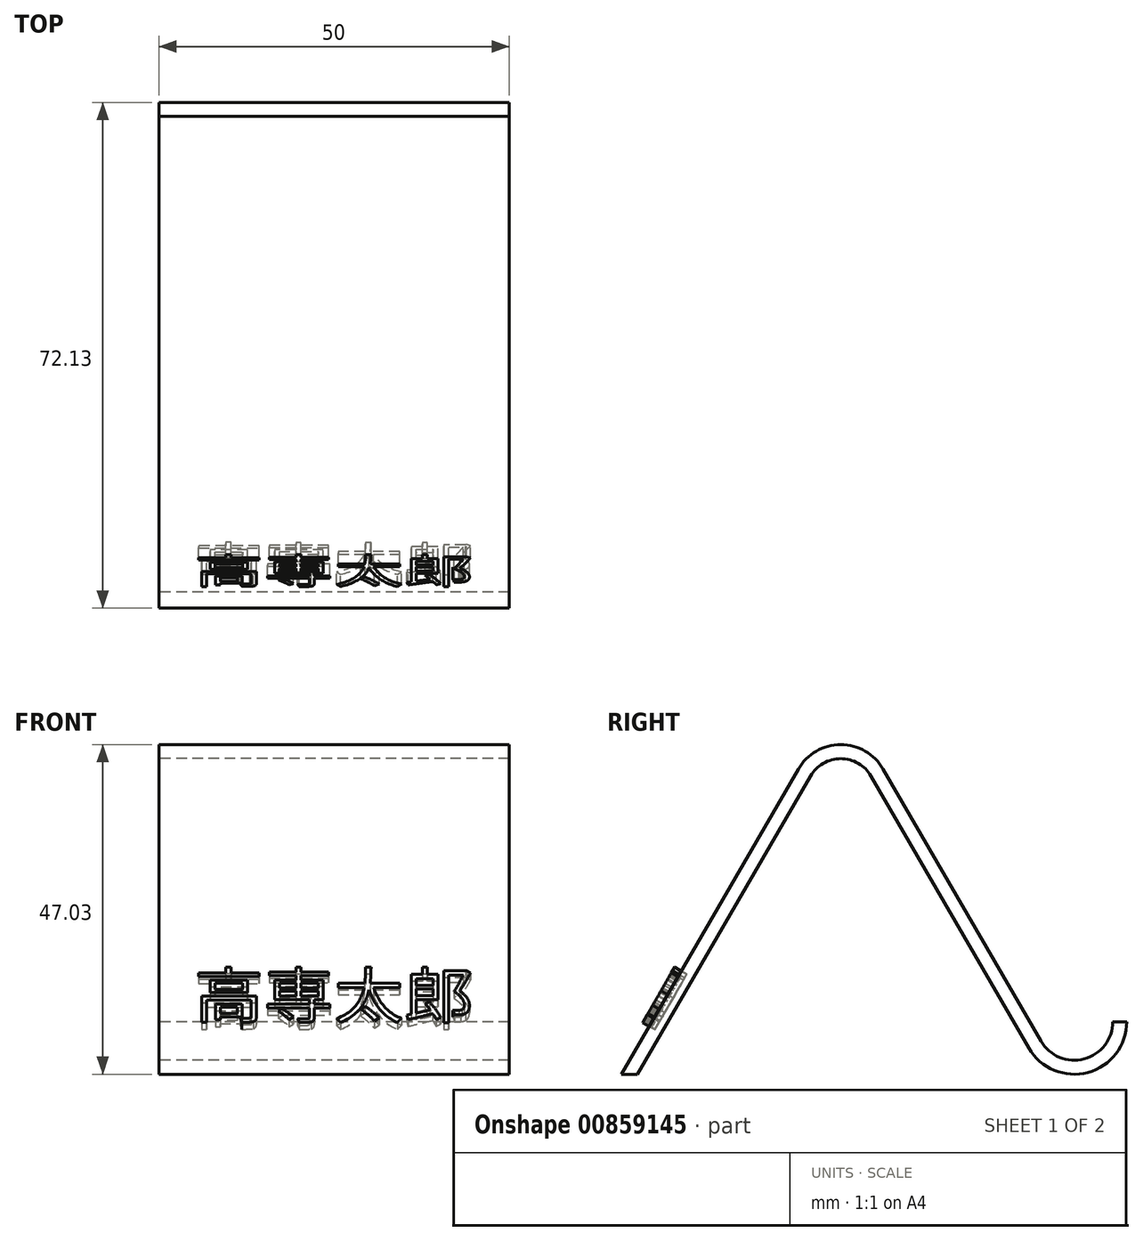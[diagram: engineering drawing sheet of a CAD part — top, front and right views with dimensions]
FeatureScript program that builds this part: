
annotation { "Feature Type Name" : "Feature", "Feature Type Description" : "" }
export const myFeature = defineFeature(function(context is Context, id is Id, definition is map)
    precondition{}
    {
        {
            var Q0;
            Q0=qCreatedBy(makeId("Right.planeOp"),FACE);
            var sketch = newSketch(context, id + "F0", { "sketchPlane" : qUnion([Q0])});
            skLineSegment(sketch, "E0", {"start": v(4.33, 42.54) * mm, "end": v(26.83, 3.74) * mm});
            skArc(sketch, "E1", {"start": v(26.83, 3.74) * mm, "mid": v(35.27, 0.26) * mm, "end": v(40.82, 7.5) * mm});
            skLineSegment(sketch, "E2", {"start": v(0, 61.22) * mm, "end": v(0, -24.36) * mm, "construction": true});
            skLineSegment(sketch, "E3", {"start": v(33.32, 7.5) * mm, "end": v(57.44, 7.5) * mm, "construction": true});
            skLineSegment(sketch, "E4", {"start": v(57.44, 0) * mm, "end": v(-52.05, 0) * mm, "construction": true});
            skLineSegment(sketch, "E5.MirrorCS", {"start": v(-4.33, 42.54) * mm, "end": v(-29, 0) * mm});
            skPoint(sketch, "E6.orphan", {"position": v(29, 0) * mm});
            skPoint(sketch, "E7.visualSharp", {"position": v(0, 50) * mm});
            skArc(sketch, "E7.filletArc", {"start": v(4.33, 42.54) * mm, "mid": v(0, 45.03) * mm, "end": v(-4.33, 42.54) * mm});
            skLineSegment(sketch, "E8.0", {"start": v(-6.06, 43.55) * mm, "end": v(-31.31, 0) * mm});
            skArc(sketch, "E8.1", {"start": v(6.06, 43.55) * mm, "mid": v(0, 47.03) * mm, "end": v(-6.06, 43.55) * mm});
            skLineSegment(sketch, "E8.2", {"start": v(6.06, 43.55) * mm, "end": v(28.56, 4.74) * mm});
            skArc(sketch, "E8.3", {"start": v(28.56, 4.74) * mm, "mid": v(34.75, 2.19) * mm, "end": v(38.82, 7.5) * mm});
            skLineSegment(sketch, "E9", {"start": v(40.82, 7.5) * mm, "end": v(38.82, 7.5) * mm});
            skLineSegment(sketch, "E10", {"start": v(-29, 0) * mm, "end": v(-31.31, 0) * mm});
            skSolve(sketch);
        }
        {
            var Q0;
            Q0 = qSketchRegion(id + "F0", true);
            extrude(context, id + "F1", {"entities" : qUnion([Q0]), "depth" : 50 * mm, "offsetDistance" : 25 * mm});
        }
        {
            var Q0;
            Q0=qCreatedBy(makeId("Front.planeOp"),FACE);
            var sketch = newSketch(context, id + "F2", { "sketchPlane" : qUnion([Q0])});
            skText(sketch, "E11", { "text": "高専太郎", "fontName": "NotoSansCJKjp-Regular.otf"});
            skLineSegment(sketch, "E12", {"start": v(25, 0) * mm, "end": v(25, 5) * mm, "construction": true});
            const initialGuessF2  = {"E11": [0.005, 0.00491, 1, 0, 0.00719]};
            skSetInitialGuess(sketch, initialGuessF2);
            skSolve(sketch);
        }
        {
            var Q0;
            Q0 = qSketchRegion(id + "F2", true);
            extrude(context, id + "F3", {"entities" : qUnion([Q0]), "depth" : 2 * mm, "offsetDistance" : 25 * mm});
        }
        {
            var Q0;
            Q0=makeQuery(id+"F3.opExtrude","SWEPT_BODY",BODY,{"disambiguationData":[OSD([sQuery(id+"F2.wireOp",EDGE,"E11.sketch_text.stroke-0"),sQuery(id+"F2.wireOp",EDGE,"E11.sketch_text.stroke-1"),sQuery(id+"F2.wireOp",EDGE,"E11.sketch_text.stroke-2"),sQuery(id+"F2.wireOp",EDGE,"E11.sketch_text.stroke-3"),sQuery(id+"F2.wireOp",EDGE,"E11.sketch_text.stroke-4"),sQuery(id+"F2.wireOp",EDGE,"E11.sketch_text.stroke-5"),sQuery(id+"F2.wireOp",EDGE,"E11.sketch_text.stroke-6"),sQuery(id+"F2.wireOp",EDGE,"E11.sketch_text.stroke-7"),sQuery(id+"F2.wireOp",EDGE,"E11.sketch_text.stroke-8"),sQuery(id+"F2.wireOp",EDGE,"E11.sketch_text.stroke-9")])]});
            var Q1;
            Q1=makeQuery(id+"F3.opExtrude","SWEPT_BODY",BODY,{"disambiguationData":[OSD([sQuery(id+"F2.wireOp",EDGE,"E11.sketch_text.stroke-10"),sQuery(id+"F2.wireOp",EDGE,"E11.sketch_text.stroke-11"),sQuery(id+"F2.wireOp",EDGE,"E11.sketch_text.stroke-12"),sQuery(id+"F2.wireOp",EDGE,"E11.sketch_text.stroke-13"),sQuery(id+"F2.wireOp",EDGE,"E11.sketch_text.stroke-14"),sQuery(id+"F2.wireOp",EDGE,"E11.sketch_text.stroke-15"),sQuery(id+"F2.wireOp",EDGE,"E11.sketch_text.stroke-16"),sQuery(id+"F2.wireOp",EDGE,"E11.sketch_text.stroke-17"),sQuery(id+"F2.wireOp",EDGE,"E11.sketch_text.stroke-18"),sQuery(id+"F2.wireOp",EDGE,"E11.sketch_text.stroke-19"),sQuery(id+"F2.wireOp",EDGE,"E11.sketch_text.stroke-20"),sQuery(id+"F2.wireOp",EDGE,"E11.sketch_text.stroke-21")])]});
            var Q2;
            Q2=makeQuery(id+"F3.opExtrude","SWEPT_BODY",BODY,{"disambiguationData":[OSD([sQuery(id+"F2.wireOp",EDGE,"E11.sketch_text.stroke-22"),sQuery(id+"F2.wireOp",EDGE,"E11.sketch_text.stroke-23"),sQuery(id+"F2.wireOp",EDGE,"E11.sketch_text.stroke-24"),sQuery(id+"F2.wireOp",EDGE,"E11.sketch_text.stroke-25"),sQuery(id+"F2.wireOp",EDGE,"E11.sketch_text.stroke-26"),sQuery(id+"F2.wireOp",EDGE,"E11.sketch_text.stroke-27"),sQuery(id+"F2.wireOp",EDGE,"E11.sketch_text.stroke-28"),sQuery(id+"F2.wireOp",EDGE,"E11.sketch_text.stroke-29")])]});
            var Q3;
            Q3=makeQuery(id+"F3.opExtrude","SWEPT_BODY",BODY,{"disambiguationData":[OSD([sQuery(id+"F2.wireOp",EDGE,"E11.sketch_text.stroke-30"),sQuery(id+"F2.wireOp",EDGE,"E11.sketch_text.stroke-31"),sQuery(id+"F2.wireOp",EDGE,"E11.sketch_text.stroke-32"),sQuery(id+"F2.wireOp",EDGE,"E11.sketch_text.stroke-33"),sQuery(id+"F2.wireOp",EDGE,"E11.sketch_text.stroke-34"),sQuery(id+"F2.wireOp",EDGE,"E11.sketch_text.stroke-35"),sQuery(id+"F2.wireOp",EDGE,"E11.sketch_text.stroke-36"),sQuery(id+"F2.wireOp",EDGE,"E11.sketch_text.stroke-37")])]});
            var Q4;
            Q4=makeQuery(id+"F3.opExtrude","SWEPT_BODY",BODY,{"disambiguationData":[OSD([sQuery(id+"F2.wireOp",EDGE,"E11.sketch_text.stroke-38"),sQuery(id+"F2.wireOp",EDGE,"E11.sketch_text.stroke-39"),sQuery(id+"F2.wireOp",EDGE,"E11.sketch_text.stroke-40"),sQuery(id+"F2.wireOp",EDGE,"E11.sketch_text.stroke-41")])]});
            var Q5;
            Q5=makeQuery(id+"F3.opExtrude","SWEPT_BODY",BODY,{"disambiguationData":[OSD([sQuery(id+"F2.wireOp",EDGE,"E11.sketch_text.stroke-42"),sQuery(id+"F2.wireOp",EDGE,"E11.sketch_text.stroke-43"),sQuery(id+"F2.wireOp",EDGE,"E11.sketch_text.stroke-44"),sQuery(id+"F2.wireOp",EDGE,"E11.sketch_text.stroke-45"),sQuery(id+"F2.wireOp",EDGE,"E11.sketch_text.stroke-46"),sQuery(id+"F2.wireOp",EDGE,"E11.sketch_text.stroke-47"),sQuery(id+"F2.wireOp",EDGE,"E11.sketch_text.stroke-48"),sQuery(id+"F2.wireOp",EDGE,"E11.sketch_text.stroke-49"),sQuery(id+"F2.wireOp",EDGE,"E11.sketch_text.stroke-50"),sQuery(id+"F2.wireOp",EDGE,"E11.sketch_text.stroke-51"),sQuery(id+"F2.wireOp",EDGE,"E11.sketch_text.stroke-52"),sQuery(id+"F2.wireOp",EDGE,"E11.sketch_text.stroke-53"),sQuery(id+"F2.wireOp",EDGE,"E11.sketch_text.stroke-54"),sQuery(id+"F2.wireOp",EDGE,"E11.sketch_text.stroke-55"),sQuery(id+"F2.wireOp",EDGE,"E11.sketch_text.stroke-56"),sQuery(id+"F2.wireOp",EDGE,"E11.sketch_text.stroke-57"),sQuery(id+"F2.wireOp",EDGE,"E11.sketch_text.stroke-58"),sQuery(id+"F2.wireOp",EDGE,"E11.sketch_text.stroke-59"),sQuery(id+"F2.wireOp",EDGE,"E11.sketch_text.stroke-60"),sQuery(id+"F2.wireOp",EDGE,"E11.sketch_text.stroke-61"),sQuery(id+"F2.wireOp",EDGE,"E11.sketch_text.stroke-62"),sQuery(id+"F2.wireOp",EDGE,"E11.sketch_text.stroke-63"),sQuery(id+"F2.wireOp",EDGE,"E11.sketch_text.stroke-64"),sQuery(id+"F2.wireOp",EDGE,"E11.sketch_text.stroke-65"),sQuery(id+"F2.wireOp",EDGE,"E11.sketch_text.stroke-66"),sQuery(id+"F2.wireOp",EDGE,"E11.sketch_text.stroke-67"),sQuery(id+"F2.wireOp",EDGE,"E11.sketch_text.stroke-68"),sQuery(id+"F2.wireOp",EDGE,"E11.sketch_text.stroke-69"),sQuery(id+"F2.wireOp",EDGE,"E11.sketch_text.stroke-70"),sQuery(id+"F2.wireOp",EDGE,"E11.sketch_text.stroke-71"),sQuery(id+"F2.wireOp",EDGE,"E11.sketch_text.stroke-72"),sQuery(id+"F2.wireOp",EDGE,"E11.sketch_text.stroke-73"),sQuery(id+"F2.wireOp",EDGE,"E11.sketch_text.stroke-74"),sQuery(id+"F2.wireOp",EDGE,"E11.sketch_text.stroke-75"),sQuery(id+"F2.wireOp",EDGE,"E11.sketch_text.stroke-76"),sQuery(id+"F2.wireOp",EDGE,"E11.sketch_text.stroke-77"),sQuery(id+"F2.wireOp",EDGE,"E11.sketch_text.stroke-78"),sQuery(id+"F2.wireOp",EDGE,"E11.sketch_text.stroke-79"),sQuery(id+"F2.wireOp",EDGE,"E11.sketch_text.stroke-80"),sQuery(id+"F2.wireOp",EDGE,"E11.sketch_text.stroke-81"),sQuery(id+"F2.wireOp",EDGE,"E11.sketch_text.stroke-82"),sQuery(id+"F2.wireOp",EDGE,"E11.sketch_text.stroke-83"),sQuery(id+"F2.wireOp",EDGE,"E11.sketch_text.stroke-84"),sQuery(id+"F2.wireOp",EDGE,"E11.sketch_text.stroke-85"),sQuery(id+"F2.wireOp",EDGE,"E11.sketch_text.stroke-86"),sQuery(id+"F2.wireOp",EDGE,"E11.sketch_text.stroke-87"),sQuery(id+"F2.wireOp",EDGE,"E11.sketch_text.stroke-88"),sQuery(id+"F2.wireOp",EDGE,"E11.sketch_text.stroke-89")])]});
            var Q6;
            Q6=makeQuery(id+"F3.opExtrude","SWEPT_BODY",BODY,{"disambiguationData":[OSD([sQuery(id+"F2.wireOp",EDGE,"E11.sketch_text.stroke-90"),sQuery(id+"F2.wireOp",EDGE,"E11.sketch_text.stroke-91"),sQuery(id+"F2.wireOp",EDGE,"E11.sketch_text.stroke-92"),sQuery(id+"F2.wireOp",EDGE,"E11.sketch_text.stroke-93")])]});
            var Q7;
            Q7=makeQuery(id+"F3.opExtrude","SWEPT_BODY",BODY,{"disambiguationData":[OSD([sQuery(id+"F2.wireOp",EDGE,"E11.sketch_text.stroke-94"),sQuery(id+"F2.wireOp",EDGE,"E11.sketch_text.stroke-95"),sQuery(id+"F2.wireOp",EDGE,"E11.sketch_text.stroke-96"),sQuery(id+"F2.wireOp",EDGE,"E11.sketch_text.stroke-97"),sQuery(id+"F2.wireOp",EDGE,"E11.sketch_text.stroke-98"),sQuery(id+"F2.wireOp",EDGE,"E11.sketch_text.stroke-99"),sQuery(id+"F2.wireOp",EDGE,"E11.sketch_text.stroke-100"),sQuery(id+"F2.wireOp",EDGE,"E11.sketch_text.stroke-101"),sQuery(id+"F2.wireOp",EDGE,"E11.sketch_text.stroke-102"),sQuery(id+"F2.wireOp",EDGE,"E11.sketch_text.stroke-103"),sQuery(id+"F2.wireOp",EDGE,"E11.sketch_text.stroke-104"),sQuery(id+"F2.wireOp",EDGE,"E11.sketch_text.stroke-105"),sQuery(id+"F2.wireOp",EDGE,"E11.sketch_text.stroke-106"),sQuery(id+"F2.wireOp",EDGE,"E11.sketch_text.stroke-107"),sQuery(id+"F2.wireOp",EDGE,"E11.sketch_text.stroke-108")])]});
            var Q8;
            Q8=makeQuery(id+"F3.opExtrude","SWEPT_BODY",BODY,{"disambiguationData":[OSD([sQuery(id+"F2.wireOp",EDGE,"E11.sketch_text.stroke-109"),sQuery(id+"F2.wireOp",EDGE,"E11.sketch_text.stroke-110"),sQuery(id+"F2.wireOp",EDGE,"E11.sketch_text.stroke-111"),sQuery(id+"F2.wireOp",EDGE,"E11.sketch_text.stroke-112"),sQuery(id+"F2.wireOp",EDGE,"E11.sketch_text.stroke-113"),sQuery(id+"F2.wireOp",EDGE,"E11.sketch_text.stroke-114"),sQuery(id+"F2.wireOp",EDGE,"E11.sketch_text.stroke-115"),sQuery(id+"F2.wireOp",EDGE,"E11.sketch_text.stroke-116"),sQuery(id+"F2.wireOp",EDGE,"E11.sketch_text.stroke-117"),sQuery(id+"F2.wireOp",EDGE,"E11.sketch_text.stroke-118"),sQuery(id+"F2.wireOp",EDGE,"E11.sketch_text.stroke-119"),sQuery(id+"F2.wireOp",EDGE,"E11.sketch_text.stroke-120"),sQuery(id+"F2.wireOp",EDGE,"E11.sketch_text.stroke-121"),sQuery(id+"F2.wireOp",EDGE,"E11.sketch_text.stroke-122"),sQuery(id+"F2.wireOp",EDGE,"E11.sketch_text.stroke-123"),sQuery(id+"F2.wireOp",EDGE,"E11.sketch_text.stroke-124"),sQuery(id+"F2.wireOp",EDGE,"E11.sketch_text.stroke-125"),sQuery(id+"F2.wireOp",EDGE,"E11.sketch_text.stroke-126"),sQuery(id+"F2.wireOp",EDGE,"E11.sketch_text.stroke-127"),sQuery(id+"F2.wireOp",EDGE,"E11.sketch_text.stroke-128"),sQuery(id+"F2.wireOp",EDGE,"E11.sketch_text.stroke-129"),sQuery(id+"F2.wireOp",EDGE,"E11.sketch_text.stroke-130"),sQuery(id+"F2.wireOp",EDGE,"E11.sketch_text.stroke-131"),sQuery(id+"F2.wireOp",EDGE,"E11.sketch_text.stroke-132"),sQuery(id+"F2.wireOp",EDGE,"E11.sketch_text.stroke-133"),sQuery(id+"F2.wireOp",EDGE,"E11.sketch_text.stroke-134")])]});
            var Q9;
            Q9=makeQuery(id+"F3.opExtrude","SWEPT_BODY",BODY,{"disambiguationData":[OSD([sQuery(id+"F2.wireOp",EDGE,"E11.sketch_text.stroke-135"),sQuery(id+"F2.wireOp",EDGE,"E11.sketch_text.stroke-136"),sQuery(id+"F2.wireOp",EDGE,"E11.sketch_text.stroke-137"),sQuery(id+"F2.wireOp",EDGE,"E11.sketch_text.stroke-138"),sQuery(id+"F2.wireOp",EDGE,"E11.sketch_text.stroke-139"),sQuery(id+"F2.wireOp",EDGE,"E11.sketch_text.stroke-140"),sQuery(id+"F2.wireOp",EDGE,"E11.sketch_text.stroke-141"),sQuery(id+"F2.wireOp",EDGE,"E11.sketch_text.stroke-142"),sQuery(id+"F2.wireOp",EDGE,"E11.sketch_text.stroke-143"),sQuery(id+"F2.wireOp",EDGE,"E11.sketch_text.stroke-144"),sQuery(id+"F2.wireOp",EDGE,"E11.sketch_text.stroke-145"),sQuery(id+"F2.wireOp",EDGE,"E11.sketch_text.stroke-146"),sQuery(id+"F2.wireOp",EDGE,"E11.sketch_text.stroke-147"),sQuery(id+"F2.wireOp",EDGE,"E11.sketch_text.stroke-148"),sQuery(id+"F2.wireOp",EDGE,"E11.sketch_text.stroke-149"),sQuery(id+"F2.wireOp",EDGE,"E11.sketch_text.stroke-150"),sQuery(id+"F2.wireOp",EDGE,"E11.sketch_text.stroke-151"),sQuery(id+"F2.wireOp",EDGE,"E11.sketch_text.stroke-152")])]});
            var Q10;
            Q10=makeQuery(id+"F1.opExtrude","SWEPT_EDGE",EDGE,{"disambiguationData":[OSD([sQuery(id+"F0.wireOp",EDGE,"E8.0"),sQuery(id+"F0.wireOp",EDGE,"E8.1")])]});
            transform(context, id + "F4", {"entities" : qUnion([Q0, Q1, Q2, Q3, Q4, Q5, Q6, Q7, Q8, Q9]), "transformType" : TransformType.ROTATION, "transformAxis" : qUnion([Q10]), "angle" : 30 * degree, "makeCopy" : false});
        }
        {
            var Q0;
            Q0=makeQuery(id+"F3.opExtrude","SWEPT_BODY",BODY,{"disambiguationData":[OSD([sQuery(id+"F2.wireOp",EDGE,"E11.sketch_text.stroke-0"),sQuery(id+"F2.wireOp",EDGE,"E11.sketch_text.stroke-1"),sQuery(id+"F2.wireOp",EDGE,"E11.sketch_text.stroke-2"),sQuery(id+"F2.wireOp",EDGE,"E11.sketch_text.stroke-3"),sQuery(id+"F2.wireOp",EDGE,"E11.sketch_text.stroke-4"),sQuery(id+"F2.wireOp",EDGE,"E11.sketch_text.stroke-5"),sQuery(id+"F2.wireOp",EDGE,"E11.sketch_text.stroke-6"),sQuery(id+"F2.wireOp",EDGE,"E11.sketch_text.stroke-7"),sQuery(id+"F2.wireOp",EDGE,"E11.sketch_text.stroke-8"),sQuery(id+"F2.wireOp",EDGE,"E11.sketch_text.stroke-9")])]});
            var Q1;
            Q1=makeQuery(id+"F3.opExtrude","SWEPT_BODY",BODY,{"disambiguationData":[OSD([sQuery(id+"F2.wireOp",EDGE,"E11.sketch_text.stroke-10"),sQuery(id+"F2.wireOp",EDGE,"E11.sketch_text.stroke-11"),sQuery(id+"F2.wireOp",EDGE,"E11.sketch_text.stroke-12"),sQuery(id+"F2.wireOp",EDGE,"E11.sketch_text.stroke-13"),sQuery(id+"F2.wireOp",EDGE,"E11.sketch_text.stroke-14"),sQuery(id+"F2.wireOp",EDGE,"E11.sketch_text.stroke-15"),sQuery(id+"F2.wireOp",EDGE,"E11.sketch_text.stroke-16"),sQuery(id+"F2.wireOp",EDGE,"E11.sketch_text.stroke-17"),sQuery(id+"F2.wireOp",EDGE,"E11.sketch_text.stroke-18"),sQuery(id+"F2.wireOp",EDGE,"E11.sketch_text.stroke-19"),sQuery(id+"F2.wireOp",EDGE,"E11.sketch_text.stroke-20"),sQuery(id+"F2.wireOp",EDGE,"E11.sketch_text.stroke-21")])]});
            var Q2;
            Q2=makeQuery(id+"F3.opExtrude","SWEPT_BODY",BODY,{"disambiguationData":[OSD([sQuery(id+"F2.wireOp",EDGE,"E11.sketch_text.stroke-22"),sQuery(id+"F2.wireOp",EDGE,"E11.sketch_text.stroke-23"),sQuery(id+"F2.wireOp",EDGE,"E11.sketch_text.stroke-24"),sQuery(id+"F2.wireOp",EDGE,"E11.sketch_text.stroke-25"),sQuery(id+"F2.wireOp",EDGE,"E11.sketch_text.stroke-26"),sQuery(id+"F2.wireOp",EDGE,"E11.sketch_text.stroke-27"),sQuery(id+"F2.wireOp",EDGE,"E11.sketch_text.stroke-28"),sQuery(id+"F2.wireOp",EDGE,"E11.sketch_text.stroke-29")])]});
            var Q3;
            Q3=makeQuery(id+"F3.opExtrude","SWEPT_BODY",BODY,{"disambiguationData":[OSD([sQuery(id+"F2.wireOp",EDGE,"E11.sketch_text.stroke-30"),sQuery(id+"F2.wireOp",EDGE,"E11.sketch_text.stroke-31"),sQuery(id+"F2.wireOp",EDGE,"E11.sketch_text.stroke-32"),sQuery(id+"F2.wireOp",EDGE,"E11.sketch_text.stroke-33"),sQuery(id+"F2.wireOp",EDGE,"E11.sketch_text.stroke-34"),sQuery(id+"F2.wireOp",EDGE,"E11.sketch_text.stroke-35"),sQuery(id+"F2.wireOp",EDGE,"E11.sketch_text.stroke-36"),sQuery(id+"F2.wireOp",EDGE,"E11.sketch_text.stroke-37")])]});
            var Q4;
            Q4=makeQuery(id+"F3.opExtrude","SWEPT_BODY",BODY,{"disambiguationData":[OSD([sQuery(id+"F2.wireOp",EDGE,"E11.sketch_text.stroke-38"),sQuery(id+"F2.wireOp",EDGE,"E11.sketch_text.stroke-39"),sQuery(id+"F2.wireOp",EDGE,"E11.sketch_text.stroke-40"),sQuery(id+"F2.wireOp",EDGE,"E11.sketch_text.stroke-41")])]});
            var Q5;
            Q5=makeQuery(id+"F3.opExtrude","SWEPT_BODY",BODY,{"disambiguationData":[OSD([sQuery(id+"F2.wireOp",EDGE,"E11.sketch_text.stroke-42"),sQuery(id+"F2.wireOp",EDGE,"E11.sketch_text.stroke-43"),sQuery(id+"F2.wireOp",EDGE,"E11.sketch_text.stroke-44"),sQuery(id+"F2.wireOp",EDGE,"E11.sketch_text.stroke-45"),sQuery(id+"F2.wireOp",EDGE,"E11.sketch_text.stroke-46"),sQuery(id+"F2.wireOp",EDGE,"E11.sketch_text.stroke-47"),sQuery(id+"F2.wireOp",EDGE,"E11.sketch_text.stroke-48"),sQuery(id+"F2.wireOp",EDGE,"E11.sketch_text.stroke-49"),sQuery(id+"F2.wireOp",EDGE,"E11.sketch_text.stroke-50"),sQuery(id+"F2.wireOp",EDGE,"E11.sketch_text.stroke-51"),sQuery(id+"F2.wireOp",EDGE,"E11.sketch_text.stroke-52"),sQuery(id+"F2.wireOp",EDGE,"E11.sketch_text.stroke-53"),sQuery(id+"F2.wireOp",EDGE,"E11.sketch_text.stroke-54"),sQuery(id+"F2.wireOp",EDGE,"E11.sketch_text.stroke-55"),sQuery(id+"F2.wireOp",EDGE,"E11.sketch_text.stroke-56"),sQuery(id+"F2.wireOp",EDGE,"E11.sketch_text.stroke-57"),sQuery(id+"F2.wireOp",EDGE,"E11.sketch_text.stroke-58"),sQuery(id+"F2.wireOp",EDGE,"E11.sketch_text.stroke-59"),sQuery(id+"F2.wireOp",EDGE,"E11.sketch_text.stroke-60"),sQuery(id+"F2.wireOp",EDGE,"E11.sketch_text.stroke-61"),sQuery(id+"F2.wireOp",EDGE,"E11.sketch_text.stroke-62"),sQuery(id+"F2.wireOp",EDGE,"E11.sketch_text.stroke-63"),sQuery(id+"F2.wireOp",EDGE,"E11.sketch_text.stroke-64"),sQuery(id+"F2.wireOp",EDGE,"E11.sketch_text.stroke-65"),sQuery(id+"F2.wireOp",EDGE,"E11.sketch_text.stroke-66"),sQuery(id+"F2.wireOp",EDGE,"E11.sketch_text.stroke-67"),sQuery(id+"F2.wireOp",EDGE,"E11.sketch_text.stroke-68"),sQuery(id+"F2.wireOp",EDGE,"E11.sketch_text.stroke-69"),sQuery(id+"F2.wireOp",EDGE,"E11.sketch_text.stroke-70"),sQuery(id+"F2.wireOp",EDGE,"E11.sketch_text.stroke-71"),sQuery(id+"F2.wireOp",EDGE,"E11.sketch_text.stroke-72"),sQuery(id+"F2.wireOp",EDGE,"E11.sketch_text.stroke-73"),sQuery(id+"F2.wireOp",EDGE,"E11.sketch_text.stroke-74"),sQuery(id+"F2.wireOp",EDGE,"E11.sketch_text.stroke-75"),sQuery(id+"F2.wireOp",EDGE,"E11.sketch_text.stroke-76"),sQuery(id+"F2.wireOp",EDGE,"E11.sketch_text.stroke-77"),sQuery(id+"F2.wireOp",EDGE,"E11.sketch_text.stroke-78"),sQuery(id+"F2.wireOp",EDGE,"E11.sketch_text.stroke-79"),sQuery(id+"F2.wireOp",EDGE,"E11.sketch_text.stroke-80"),sQuery(id+"F2.wireOp",EDGE,"E11.sketch_text.stroke-81"),sQuery(id+"F2.wireOp",EDGE,"E11.sketch_text.stroke-82"),sQuery(id+"F2.wireOp",EDGE,"E11.sketch_text.stroke-83"),sQuery(id+"F2.wireOp",EDGE,"E11.sketch_text.stroke-84"),sQuery(id+"F2.wireOp",EDGE,"E11.sketch_text.stroke-85"),sQuery(id+"F2.wireOp",EDGE,"E11.sketch_text.stroke-86"),sQuery(id+"F2.wireOp",EDGE,"E11.sketch_text.stroke-87"),sQuery(id+"F2.wireOp",EDGE,"E11.sketch_text.stroke-88"),sQuery(id+"F2.wireOp",EDGE,"E11.sketch_text.stroke-89")])]});
            var Q6;
            Q6=makeQuery(id+"F3.opExtrude","SWEPT_BODY",BODY,{"disambiguationData":[OSD([sQuery(id+"F2.wireOp",EDGE,"E11.sketch_text.stroke-90"),sQuery(id+"F2.wireOp",EDGE,"E11.sketch_text.stroke-91"),sQuery(id+"F2.wireOp",EDGE,"E11.sketch_text.stroke-92"),sQuery(id+"F2.wireOp",EDGE,"E11.sketch_text.stroke-93")])]});
            var Q7;
            Q7=makeQuery(id+"F3.opExtrude","SWEPT_BODY",BODY,{"disambiguationData":[OSD([sQuery(id+"F2.wireOp",EDGE,"E11.sketch_text.stroke-94"),sQuery(id+"F2.wireOp",EDGE,"E11.sketch_text.stroke-95"),sQuery(id+"F2.wireOp",EDGE,"E11.sketch_text.stroke-96"),sQuery(id+"F2.wireOp",EDGE,"E11.sketch_text.stroke-97"),sQuery(id+"F2.wireOp",EDGE,"E11.sketch_text.stroke-98"),sQuery(id+"F2.wireOp",EDGE,"E11.sketch_text.stroke-99"),sQuery(id+"F2.wireOp",EDGE,"E11.sketch_text.stroke-100"),sQuery(id+"F2.wireOp",EDGE,"E11.sketch_text.stroke-101"),sQuery(id+"F2.wireOp",EDGE,"E11.sketch_text.stroke-102"),sQuery(id+"F2.wireOp",EDGE,"E11.sketch_text.stroke-103"),sQuery(id+"F2.wireOp",EDGE,"E11.sketch_text.stroke-104"),sQuery(id+"F2.wireOp",EDGE,"E11.sketch_text.stroke-105"),sQuery(id+"F2.wireOp",EDGE,"E11.sketch_text.stroke-106"),sQuery(id+"F2.wireOp",EDGE,"E11.sketch_text.stroke-107"),sQuery(id+"F2.wireOp",EDGE,"E11.sketch_text.stroke-108")])]});
            var Q8;
            Q8=makeQuery(id+"F3.opExtrude","SWEPT_BODY",BODY,{"disambiguationData":[OSD([sQuery(id+"F2.wireOp",EDGE,"E11.sketch_text.stroke-109"),sQuery(id+"F2.wireOp",EDGE,"E11.sketch_text.stroke-110"),sQuery(id+"F2.wireOp",EDGE,"E11.sketch_text.stroke-111"),sQuery(id+"F2.wireOp",EDGE,"E11.sketch_text.stroke-112"),sQuery(id+"F2.wireOp",EDGE,"E11.sketch_text.stroke-113"),sQuery(id+"F2.wireOp",EDGE,"E11.sketch_text.stroke-114"),sQuery(id+"F2.wireOp",EDGE,"E11.sketch_text.stroke-115"),sQuery(id+"F2.wireOp",EDGE,"E11.sketch_text.stroke-116"),sQuery(id+"F2.wireOp",EDGE,"E11.sketch_text.stroke-117"),sQuery(id+"F2.wireOp",EDGE,"E11.sketch_text.stroke-118"),sQuery(id+"F2.wireOp",EDGE,"E11.sketch_text.stroke-119"),sQuery(id+"F2.wireOp",EDGE,"E11.sketch_text.stroke-120"),sQuery(id+"F2.wireOp",EDGE,"E11.sketch_text.stroke-121"),sQuery(id+"F2.wireOp",EDGE,"E11.sketch_text.stroke-122"),sQuery(id+"F2.wireOp",EDGE,"E11.sketch_text.stroke-123"),sQuery(id+"F2.wireOp",EDGE,"E11.sketch_text.stroke-124"),sQuery(id+"F2.wireOp",EDGE,"E11.sketch_text.stroke-125"),sQuery(id+"F2.wireOp",EDGE,"E11.sketch_text.stroke-126"),sQuery(id+"F2.wireOp",EDGE,"E11.sketch_text.stroke-127"),sQuery(id+"F2.wireOp",EDGE,"E11.sketch_text.stroke-128"),sQuery(id+"F2.wireOp",EDGE,"E11.sketch_text.stroke-129"),sQuery(id+"F2.wireOp",EDGE,"E11.sketch_text.stroke-130"),sQuery(id+"F2.wireOp",EDGE,"E11.sketch_text.stroke-131"),sQuery(id+"F2.wireOp",EDGE,"E11.sketch_text.stroke-132"),sQuery(id+"F2.wireOp",EDGE,"E11.sketch_text.stroke-133"),sQuery(id+"F2.wireOp",EDGE,"E11.sketch_text.stroke-134")])]});
            var Q9;
            Q9=makeQuery(id+"F3.opExtrude","SWEPT_BODY",BODY,{"disambiguationData":[OSD([sQuery(id+"F2.wireOp",EDGE,"E11.sketch_text.stroke-135"),sQuery(id+"F2.wireOp",EDGE,"E11.sketch_text.stroke-136"),sQuery(id+"F2.wireOp",EDGE,"E11.sketch_text.stroke-137"),sQuery(id+"F2.wireOp",EDGE,"E11.sketch_text.stroke-138"),sQuery(id+"F2.wireOp",EDGE,"E11.sketch_text.stroke-139"),sQuery(id+"F2.wireOp",EDGE,"E11.sketch_text.stroke-140"),sQuery(id+"F2.wireOp",EDGE,"E11.sketch_text.stroke-141"),sQuery(id+"F2.wireOp",EDGE,"E11.sketch_text.stroke-142"),sQuery(id+"F2.wireOp",EDGE,"E11.sketch_text.stroke-143"),sQuery(id+"F2.wireOp",EDGE,"E11.sketch_text.stroke-144"),sQuery(id+"F2.wireOp",EDGE,"E11.sketch_text.stroke-145"),sQuery(id+"F2.wireOp",EDGE,"E11.sketch_text.stroke-146"),sQuery(id+"F2.wireOp",EDGE,"E11.sketch_text.stroke-147"),sQuery(id+"F2.wireOp",EDGE,"E11.sketch_text.stroke-148"),sQuery(id+"F2.wireOp",EDGE,"E11.sketch_text.stroke-149"),sQuery(id+"F2.wireOp",EDGE,"E11.sketch_text.stroke-150"),sQuery(id+"F2.wireOp",EDGE,"E11.sketch_text.stroke-151"),sQuery(id+"F2.wireOp",EDGE,"E11.sketch_text.stroke-152")])]});
            transform(context, id + "F5", {"entities" : qUnion([Q0, Q1, Q2, Q3, Q4, Q5, Q6, Q7, Q8, Q9]), "transformType" : TransformType.TRANSLATION_3D, "dx" : 0 * mm, "dy" : -6 * mm, "dz" : 0 * mm, "makeCopy" : false});
        }
    });
